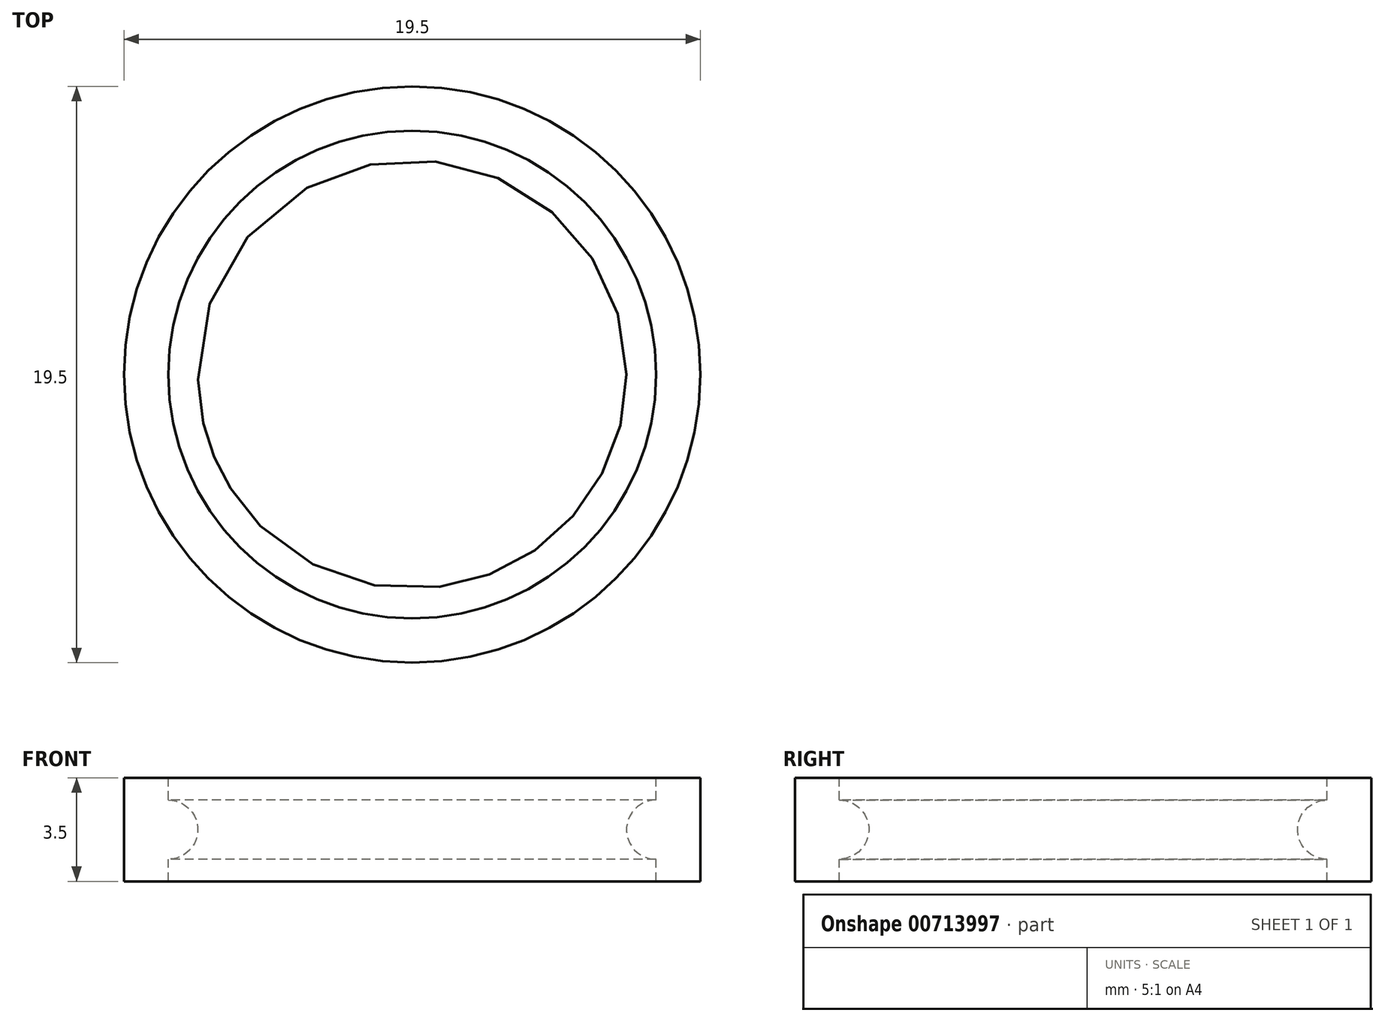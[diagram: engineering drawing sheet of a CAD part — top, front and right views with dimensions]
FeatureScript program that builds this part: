
annotation { "Feature Type Name" : "Feature", "Feature Type Description" : "" }
export const myFeature = defineFeature(function(context is Context, id is Id, definition is map)
    precondition{}
    {
        {
            var Q0;
            Q0=qCreatedBy(makeId("Right.planeOp"),FACE);
            var sketch = newSketch(context, id + "F0", { "sketchPlane" : qUnion([Q0])});
            skLineSegment(sketch, "E0", {"start": v(-3.84, 0) * mm, "end": v(3.5, 0) * mm, "construction": true});
            skLineSegment(sketch, "E1", {"start": v(-2.73, 0) * mm, "end": v(-2.73, 1.75) * mm});
            skLineSegment(sketch, "E2", {"start": v(-2.73, 1.75) * mm, "end": v(-1.23, 1.75) * mm});
            skLineSegment(sketch, "E3", {"start": v(-1.23, 1.75) * mm, "end": v(-1.23, 1) * mm});
            skLineSegment(sketch, "E4", {"start": v(-1.23, 1) * mm, "end": v(-1.23, 0) * mm, "construction": true});
            skArc(sketch, "E5", {"start": v(-1.23, 1) * mm, "mid": v(-0.52, 0.7) * mm, "end": v(-0.23, 0) * mm});
            skLineSegment(sketch, "E6.MirrorCS", {"start": v(-2.73, 0) * mm, "end": v(-2.73, -1.75) * mm});
            skLineSegment(sketch, "E7.MirrorCS", {"start": v(-2.73, -1.75) * mm, "end": v(-1.23, -1.75) * mm});
            skLineSegment(sketch, "E8.MirrorCS", {"start": v(-1.23, -1.75) * mm, "end": v(-1.23, -1) * mm});
            skArc(sketch, "E9.MirrorCS", {"start": v(-1.23, -1) * mm, "mid": v(-0.52, -0.7) * mm, "end": v(-0.23, 0) * mm});
            skLineSegment(sketch, "E10", {"start": v(7.02, 3.47) * mm, "end": v(7.02, -3.14) * mm, "construction": true});
            skSolve(sketch);
        }
        {
            var Q0;
            Q0=makeQuery(id+"F0.imprint","IMPRINT",FACE,{"disambiguationData":[TD([[makeQuery(id+"F0.imprint","IMPRINT",EDGE,{"derivedFrom":sQuery(id+"F0.wireOp",EDGE,"E1")}),-1.0]])]});
            var Q1;
            Q1=sQuery(id+"F0.wireOp",EDGE,"E10");
            revolve(context, id + "F1", {"surfaceOperationType" : NewSurfaceOperationType.NEW, "entities" : qUnion([Q0]), "axis" : qUnion([Q1]), "revolveType" : RevolveType.FULL});
        }
    });
